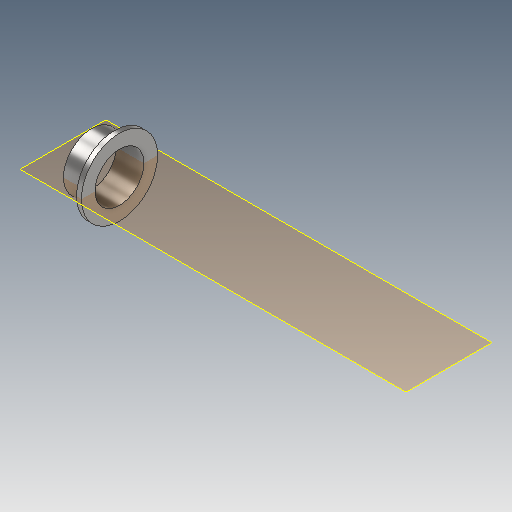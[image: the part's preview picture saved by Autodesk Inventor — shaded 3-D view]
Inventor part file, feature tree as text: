
AUTODESK INVENTOR PART (.ipt)
format: ipt  version: 2025 (Build 290162000, 162)  size: 110,080 bytes
history: native  units: mm
features: other x8, reference x4, plane x1, revolve x1, sketch x1
ambient origin geometry x8: Origin, YZ Plane, XZ Plane, XY Plane, X Axis, Y Axis, Z Axis, Center Point
bodies: 实体1 (feature_tree)
feature tree (15):
  plane  "工作平面1"
  revolve  "旋转1"  [1 undecoded]
  sketch  "草图1"  dims[d0=4.0mm d1=10.0mm d2=5.0mm d3=90.0deg]
  reference  "参考1"
  reference  "参考2"
  reference  "参考3"
  reference  "参考4"
  other  "齿轮箱.iam"
  other  "低速轴:1"
  other  "轴承:1"
  other  "滚动轴承 GB/T 276-1994 60000 和 160000 型 6010:1"
  other  "低速齿轮:1"
  other  "正齿轮:1"
  other  "正齿轮2:1"
  other  "轴:1"
note: 1 required parameter value undecoded (feature->parameter linkage not recoverable at this tier; creation-order binding heuristic only, values carry confidence <= 0.55)
